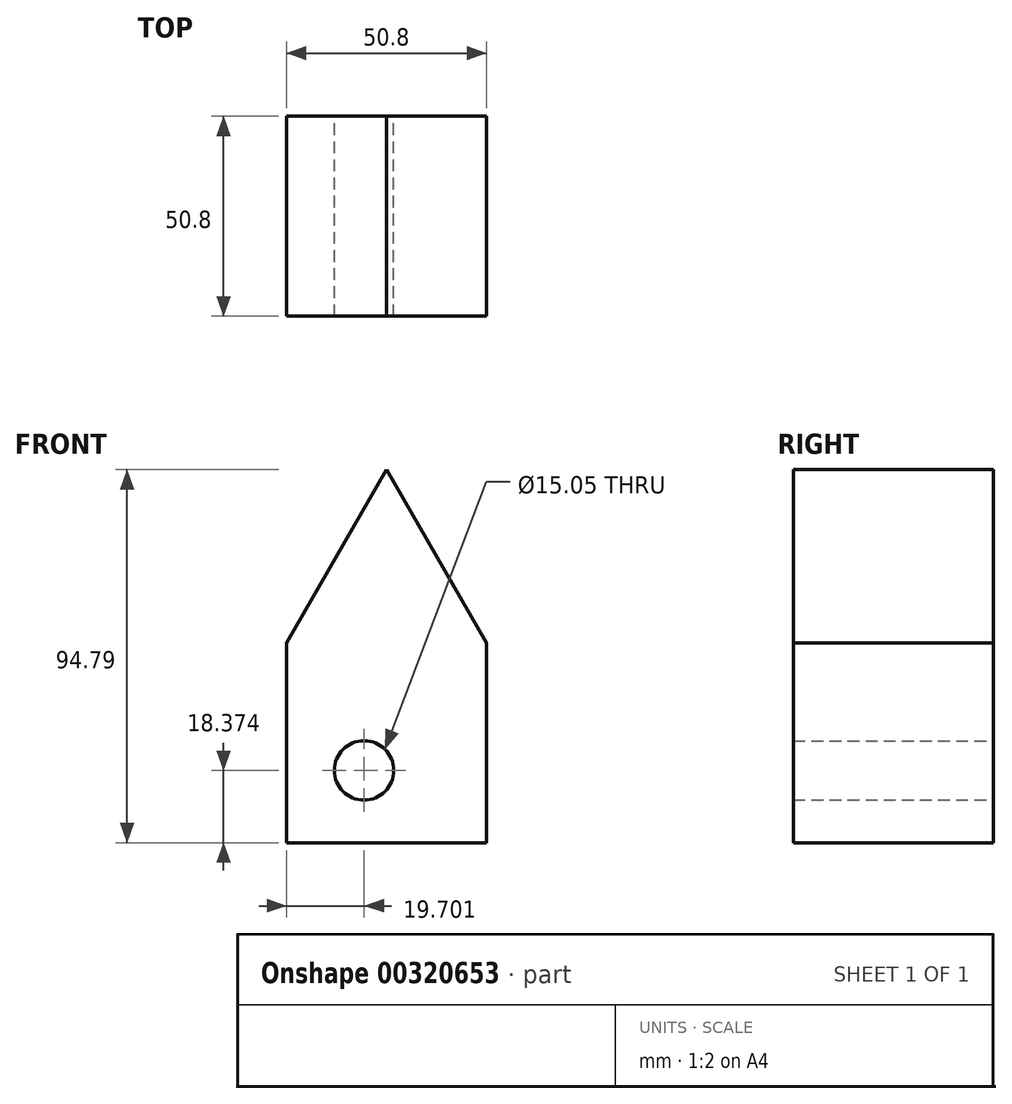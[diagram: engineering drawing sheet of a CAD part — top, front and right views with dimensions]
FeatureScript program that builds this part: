
annotation { "Feature Type Name" : "Feature", "Feature Type Description" : "" }
export const myFeature = defineFeature(function(context is Context, id is Id, definition is map)
    precondition{}
    {
        {
            var Q0;
            Q0=qCreatedBy(makeId("Front.planeOp"),FACE);
            var sketch = newSketch(context, id + "F0", { "sketchPlane" : qUnion([Q0])});
            skLineSegment(sketch, "E0.bottom", {"start": v(-25.4, -25.4) * mm, "end": v(25.4, -25.4) * mm});
            skLineSegment(sketch, "E0.top", {"start": v(-25.4, 25.4) * mm, "end": v(25.4, 25.4) * mm});
            skLineSegment(sketch, "E0.left", {"start": v(-25.4, -25.4) * mm, "end": v(-25.4, 25.4) * mm});
            skLineSegment(sketch, "E0.right", {"start": v(25.4, -25.4) * mm, "end": v(25.4, 25.4) * mm});
            skPoint(sketch, "E0.middle", {"position": v(0, 0) * mm});
            skLineSegment(sketch, "E1", {"start": v(-25.4, 25.4) * mm, "end": v(0, 69.4) * mm});
            skLineSegment(sketch, "E2", {"start": v(0, 69.4) * mm, "end": v(25.4, 25.4) * mm});
            skLineSegment(sketch, "E3", {"start": v(-5.7, 25.4) * mm, "end": v(-5.7, -25.4) * mm});
            skLineSegment(sketch, "E4", {"start": v(-25.4, -7.03) * mm, "end": v(25.4, -7.03) * mm});
            skCircle(sketch, "E5", {"center": v(-5.7, -7.03) * mm, "radius": 7.53 * mm});
            skPoint(sketch, "E5.centerSnap0", {"position": v(0, -7.03) * mm});
            skSolve(sketch);
        }
        {
            var Q0;
            Q0 = qSketchRegion(id + "F0", true);
            extrude(context, id + "F1", {"entities" : qUnion([Q0]), "depth" : 50.8 * mm});
        }
    });
